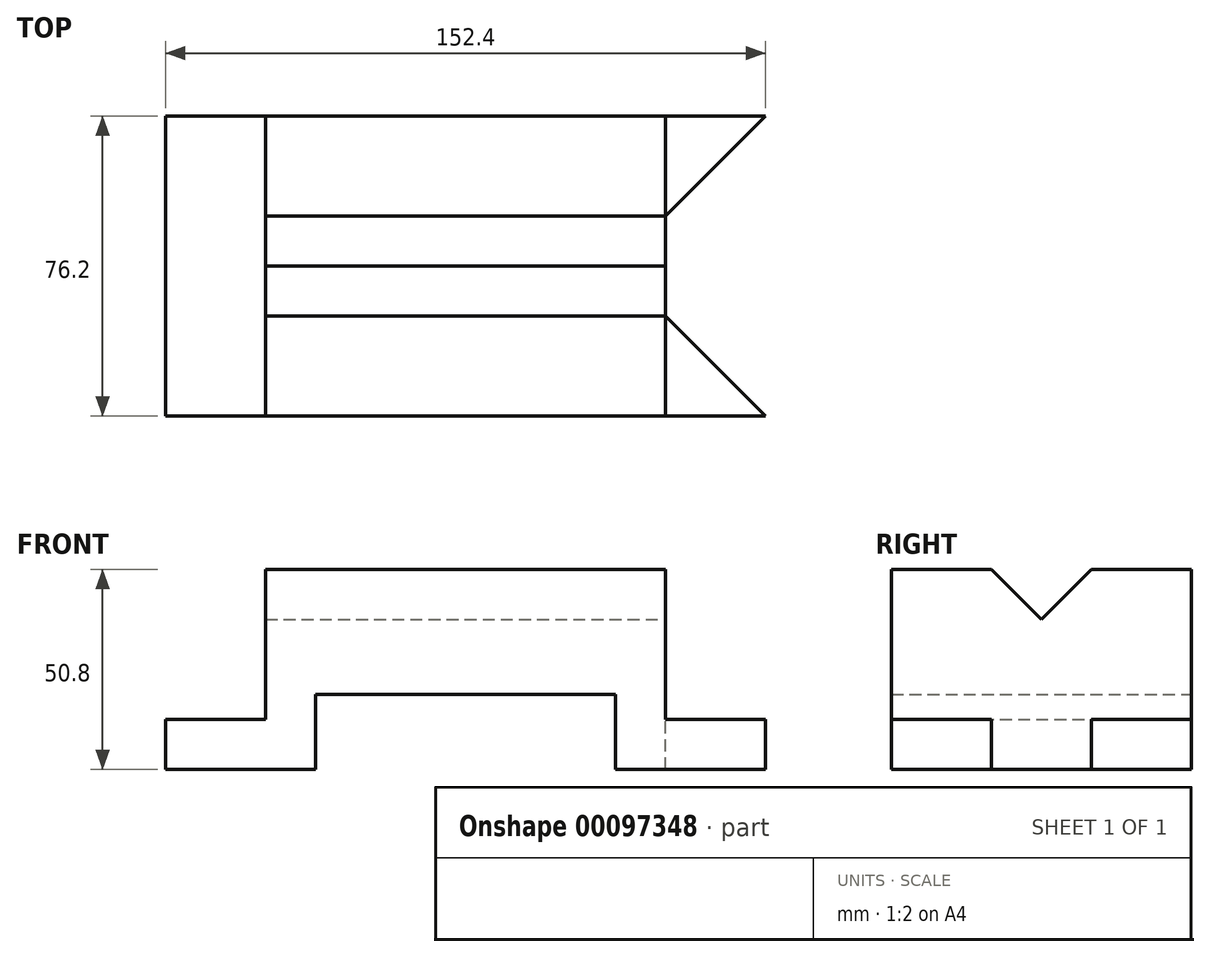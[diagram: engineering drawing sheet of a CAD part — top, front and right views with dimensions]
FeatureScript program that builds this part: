
annotation { "Feature Type Name" : "Feature", "Feature Type Description" : "" }
export const myFeature = defineFeature(function(context is Context, id is Id, definition is map)
    precondition{}
    {
        {
            var Q0;
            Q0=qCreatedBy(makeId("Front.planeOp"),FACE);
            var sketch = newSketch(context, id + "F0", { "sketchPlane" : qUnion([Q0])});
            skLineSegment(sketch, "E0", {"start": v(0, 19.05) * mm, "end": v(38.1, 19.05) * mm});
            skLineSegment(sketch, "E1", {"start": v(38.1, 19.05) * mm, "end": v(38.1, 0) * mm});
            skLineSegment(sketch, "E2", {"start": v(38.1, 0) * mm, "end": v(76.2, 0) * mm});
            skLineSegment(sketch, "E3", {"start": v(76.2, 0) * mm, "end": v(76.2, 12.7) * mm});
            skLineSegment(sketch, "E4", {"start": v(76.2, 12.7) * mm, "end": v(50.8, 12.7) * mm});
            skLineSegment(sketch, "E5", {"start": v(50.8, 12.7) * mm, "end": v(50.8, 50.8) * mm});
            skLineSegment(sketch, "E6", {"start": v(50.8, 50.8) * mm, "end": v(-50.8, 50.8) * mm});
            skLineSegment(sketch, "E7", {"start": v(-50.8, 50.8) * mm, "end": v(-50.8, 12.7) * mm});
            skLineSegment(sketch, "E8", {"start": v(-50.8, 12.7) * mm, "end": v(-76.2, 12.7) * mm});
            skLineSegment(sketch, "E9", {"start": v(-76.2, 12.7) * mm, "end": v(-76.2, 0) * mm});
            skLineSegment(sketch, "E10", {"start": v(-76.2, 0) * mm, "end": v(-38.1, 0) * mm});
            skLineSegment(sketch, "E11", {"start": v(-38.1, 0) * mm, "end": v(-38.1, 19.05) * mm});
            skLineSegment(sketch, "E12", {"start": v(-38.1, 19.05) * mm, "end": v(0, 19.05) * mm});
            skSolve(sketch);
        }
        {
            var Q0;
            Q0=makeQuery(id+"F0.imprint","IMPRINT",FACE,{"disambiguationData":[TD([[makeQuery(id+"F0.imprint","IMPRINT",EDGE,{"derivedFrom":sQuery(id+"F0.wireOp",EDGE,"E0")}),1.0]])]});
            extrude(context, id + "F1", {"entities" : qUnion([Q0]), "depth" : 76.2 * mm, "symmetric" : true});
        }
        {
            var Q0;
            Q0=makeQuery(id+"F1.opExtrude","SWEPT_FACE",FACE,{"disambiguationData":[OSD([sQuery(id+"F0.wireOp",EDGE,"E4")])]});
            var sketch = newSketch(context, id + "F2", { "sketchPlane" : qUnion([Q0])});
            skLineSegment(sketch, "E13", {"start": v(76.2, -38.1) * mm, "end": v(50.8, -12.7) * mm});
            skLineSegment(sketch, "E14", {"start": v(50.8, -12.7) * mm, "end": v(50.8, 12.7) * mm});
            skLineSegment(sketch, "E15", {"start": v(50.8, 12.7) * mm, "end": v(76.2, 38.1) * mm});
            skLineSegment(sketch, "E16", {"start": v(76.2, 38.1) * mm, "end": v(76.2, -38.1) * mm});
            skSolve(sketch);
        }
        {
            var Q0;
            Q0=makeQuery(id+"F2.imprint","IMPRINT",FACE,{"disambiguationData":[TD([[makeQuery(id+"F2.imprint","IMPRINT",EDGE,{"derivedFrom":sQuery(id+"F2.wireOp",EDGE,"E13")}),-1.0]])]});
            extrude(context, id + "F3", {"entities" : qUnion([Q0]), "operationType" : NewBodyOperationType.REMOVE, "endBound" : BoundingType.THROUGH_ALL, "oppositeDirection" : true, "depth" : 25.4 * mm});
        }
        {
            var Q0;
            Q0=makeQuery(id+"F3.boolean.opBoolean","MERGE",FACE,{"derivedFrom":[makeQuery(id+"F1.opExtrude","SWEPT_FACE",FACE,{"disambiguationData":[OSD([sQuery(id+"F0.wireOp",EDGE,"E5")])]}),makeQuery(id+"F3.opExtrude","SWEPT_FACE",FACE,{"disambiguationData":[OSD([sQuery(id+"F2.wireOp",EDGE,"E14")])]})]});
            var sketch = newSketch(context, id + "F4", { "sketchPlane" : qUnion([Q0])});
            skLineSegment(sketch, "E17", {"start": v(-12.7, 50.8) * mm, "end": v(0, 38.1) * mm});
            skPoint(sketch, "E17.endSnap0", {"position": v(0, 50.8) * mm});
            skLineSegment(sketch, "E18", {"start": v(0, 38.1) * mm, "end": v(12.7, 50.8) * mm});
            skLineSegment(sketch, "E19", {"start": v(12.7, 50.8) * mm, "end": v(-12.7, 50.8) * mm});
            skSolve(sketch);
        }
        {
            var Q0;
            Q0=makeQuery(id+"F4.imprint","IMPRINT",FACE,{"disambiguationData":[TD([[makeQuery(id+"F4.imprint","IMPRINT",EDGE,{"derivedFrom":sQuery(id+"F4.wireOp",EDGE,"E17")}),1.0]])]});
            extrude(context, id + "F5", {"entities" : qUnion([Q0]), "operationType" : NewBodyOperationType.REMOVE, "endBound" : BoundingType.THROUGH_ALL, "oppositeDirection" : true, "depth" : 25.4 * mm});
        }
    });
